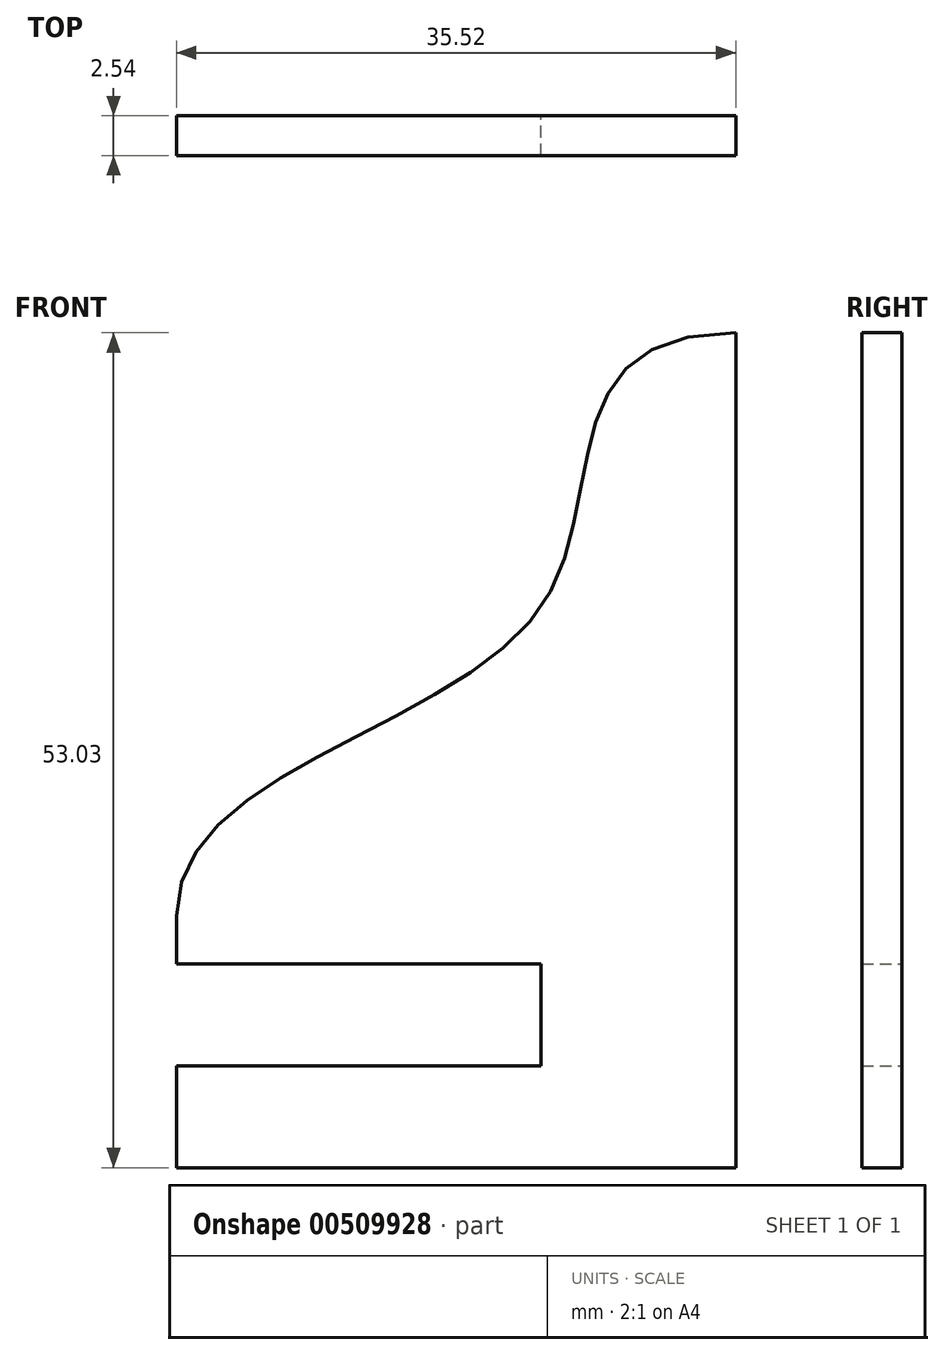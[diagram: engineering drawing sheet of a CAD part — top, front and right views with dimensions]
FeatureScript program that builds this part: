
annotation { "Feature Type Name" : "Feature", "Feature Type Description" : "" }
export const myFeature = defineFeature(function(context is Context, id is Id, definition is map)
    precondition{}
    {
        {
            var Q0;
            Q0=qCreatedBy(makeId("Front.planeOp"),FACE);
            var sketch = newSketch(context, id + "F0", { "sketchPlane" : qUnion([Q0])});
            skFitSpline(sketch, "E0", {"points": [v(0, 42.91) * mm, v(-12.33, 25.55) * mm, v(-35.52, 5.86) * mm], "startDerivative": vector(-80, 0) * mm, "endDerivative": vector(0, -52.87) * mm});
            skLineSegment(sketch, "E1", {"start": v(-35.52, 5.86) * mm, "end": v(-35.52, 2.82) * mm});
            skLineSegment(sketch, "E2", {"start": v(-35.52, -10.12) * mm, "end": v(0, -10.12) * mm});
            skLineSegment(sketch, "E3", {"start": v(0, -10.12) * mm, "end": v(0, 42.91) * mm});
            skLineSegment(sketch, "E4.bottom", {"start": v(-35.52, 2.82) * mm, "end": v(-12.36, 2.82) * mm});
            skLineSegment(sketch, "E4.top", {"start": v(-35.52, -3.65) * mm, "end": v(-12.36, -3.65) * mm});
            skLineSegment(sketch, "E4.right", {"start": v(-12.36, 2.82) * mm, "end": v(-12.36, -3.65) * mm});
            skLineSegment(sketch, "E5.trimOffspring", {"start": v(-35.52, -3.65) * mm, "end": v(-35.52, -10.12) * mm});
            skSolve(sketch);
        }
        {
            var Q0;
            Q0=makeQuery(id+"F0.imprint","IMPRINT",FACE,{"disambiguationData":[TD([[makeQuery(id+"F0.imprint","IMPRINT",EDGE,{"derivedFrom":sQuery(id+"F0.wireOp",EDGE,"E0")}),1.0]])]});
            extrude(context, id + "F1", {"entities" : qUnion([Q0]), "depth" : 2.54 * mm, "offsetDistance" : 25.4 * mm});
        }
    });
